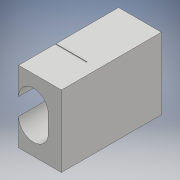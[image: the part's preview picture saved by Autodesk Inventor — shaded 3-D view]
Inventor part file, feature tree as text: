
AUTODESK INVENTOR PART (.ipt)
format: ipt  version: 2017 (Build 210142000, 142)  size: 127,488 bytes
history: native  units: mm
features: extrude x3, sketch x3
ambient origin geometry x8: Origin, YZ Plane, XZ Plane, XY Plane, X Axis, Y Axis, Z Axis, Center Point
bodies: Solid1 (feature_tree)
feature tree (6):
  extrude  "Extrusion1"  Depth=35.0mm
  extrude  "Extrusion2"  Depth=10.4mm
  extrude  "Extrusion3"  Depth=35.0mm TaperAngle=0.0deg
  sketch  "Sketch1"  dims[d0=15.0mm d1=35.0mm]
  sketch  "Sketch2"  dims[d2=25.0mm d3=0.0mm d4=10.4mm]
  sketch  "Sketch3"  dims[d5=16.4mm d6=35.0mm d7=0.0mm d8=0.2mm d9=11.0mm d10=0.0mm]
